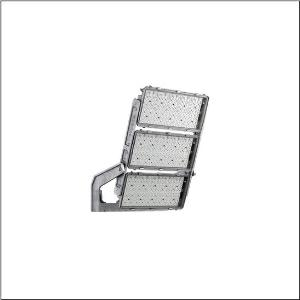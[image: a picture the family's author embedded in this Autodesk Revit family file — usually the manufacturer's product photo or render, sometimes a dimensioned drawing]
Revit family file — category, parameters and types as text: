
# Revit family: floodlight_fl_11_maxi_pro_remote___pl52_5xa779426d01ba_5366
name_source: partatom
category: Lighting Fixtures
units: mm (PartAtom-declared; Revit-internal decimal feet)

## family parameters
Cut with Voids When Loaded = No
Host = Face
Light Source = No
Part Type = Normal
Room Calculation Point = No
Round Connector Dimension = Use Diameter
Shared = No

## types (1)
- --- (1 x LED, 146220 lm, 1095.8 W, 4000K)
    Apparent Load = 1096 VA
    CIE Flux Codes = 24 55 98 100 100
    Color Rendering = 70
    Color Temperature = 4000K
    Default Elevation = 1800 mm
    Description = Floodlight FL 11  maxi  pro Remote floodlight; light control with lens of PMMA; cover panel of toughened safety glass, transparent; light distribution: PL52, asymmetric direct distribution, LEDcolour temperature: 4000K, rated luminous flux: 146.220lm, colour rendering: CRI > 70, light colour: 740; luminous efficacy: 133lm/W; brightness control: DALI 2 (1 DALI address); with terminal, 8-pole, max. 2.5mm², mains connection: 220..240V/380..400V AC, 50/60Hz, surge voltage resistance: line to ground: 10kV, ECG replaceable separately, LED unit replaceable without ESD environment, dustproof LED module, dimming range 10..100%, no afterglow with DALI off / DMX off command; 1096W floodlight with 3x LED unit of diecast aluminium, coated grey; length: 713mm / width: 651mm / height: 338mm; mounting bracket, of diecast aluminium, uncoated, natural, equipment: Longlife, protection rating (complete): IP66; insulation class (complete): insulation class I (protective earthing); certification: CE, ENEC, VDE; ball protection: ball impact resistance with accessories, impact resistance: IK07; rated ambient temperature 10°C, only for outdoor installations, permissible operating ambient temperature: -40..+40°C, permissible storage temperature: -40..+85°C; packaging unit: 1 piece

Light Distribution: PL52
    Height = 320 mm
    Lamp = 1 x LED
    Lamp Light Flux = 146220 lm
    Lamp Power = 1095.8 W
    Lamp count = 1
    Length = 1002 mm
    Luminous efficacy = 133 lm/W
    Manufacturer = Siteco
    ModVariant = No
    Model = 5XA779426D01BA
    Mounting Place = Ceiling
    Mounting Type = Surface mounted
    Number of Poles = 1
    OnlyDefault = Yes
    Power Factor = 1
    Product Name = Floodlight FL 11 maxi pro Remote | PL52
    Product group = floodlight | ceiling mounted
    ProductGroupID = 302
    Protection Class = Protection class I
    Protection Degree = IP 66
    RLX_Detail_Level = 1
    RLX_Emergency_Light_Flux = 0 lm
    RLX_Emergency_Type = 0
    RLX_Emergency_Type_DB = No
    RlxData = <blob elided: 52461 chars, md5=1aeb182f>
    Socket = socket
    Standby Power = 0 W
    System Light Flux = 146220 lm
    System Power = 1096 W
    Type Comments = factory setting: luminous flux: 100 % | dim-lin: 254 | 760 mA
    Type Image = l_1006784.jpg
    URL = http://relux.com
    VarID = @adj_066707
    Voltage = 0 V
    Weight = 0.00 kg
    Width = 655 mm

## geometry (parser evidence)
native form markers: Blend x4, Sweep x13
no freeform markers — native parametric forms only
